# Revit family: IS_Tipica_T2378_BIM_FR
name_source: partatom
category: Plumbing Fixtures
revit_build: Autodesk Revit 2017 (Build: 20160225_1515(x64)
units: mm (PartAtom-declared; Revit-internal decimal feet)

## family parameters
Always vertical = No
Cut with Voids When Loaded = No
OmniClass Number = 23.45.05.14.21.11
OmniClass Title = Bath/Shower Units
Part Type = Normal
Room Calculation Point = No
Round Connector Dimension = Use Diameter
Shared = No
Work Plane-Based = No

## types (2) — shared parameters
Accessoires = www.idealspec.fr
Auteur = Ideal Standard
BIMobject category = Shower screens
BIMobject category code = sanitary-shower-screens
BIMobject main category = Sanitary
BIMobject main category code = sanitary
BOSUseNativeGeometries = 1
Brand url = www.idealspec.fr
Caractéristiques = TIPICA A SHW ENCL 80X80 TRANSP.WHITE
CodeBarre = 8014140362234
Conformité = NF
ConseilsDInstallation = 0
Couleur = Argent, clair
Date of publishing = 2018_07_24
DateDeCréation = 2018_07_24
Description = TIPICA A Cabine de douche 80 x 80 cm verre transparent
Dimensions = 820 x 820 x 1850 mm
EAN code = https://8014140362234
Edition number = 1
Espace = Interne
Finition = Argent, clair
Forme = Complexe
Hauteur = 1850 mm  [stored 6.06955 ft]
IFC Classification = Sanitary Terminal
IfcExportAs = SHOWER ENCLOSURES
IfcExportType = IfcSanitaryTerminalType
InformationsProduit = www.idealspec.fr
Installation instructions = http://www.idealspec.fr
Largeur = 820 mm
Longueur = 820 mm
Manufacturer name = Ideal Standard
Marque = Ideal Standard
Material main = Glass
Matériel = Glass
NBS Reference Code = 35-06-79
NBS Reference Description = Shower Enclosures
Nominal height = 1850
Nominal width = 795
OmniClass Code = 23-31 17 00
OmniClass Description = Showers
Product Guid = fd2bb281-8874-41ba-9d1a-fc2fd3af9e73
Product SKU = T2378
Product certification = http://www.idealspec.fr
Product data url = https://bimobject.com
Product family = Sanitary
Product group = Shower enclosures
Product name = TIPICA A SHW ENCL 80X80 TRANSP.WHITE
Product url = http://www.idealstandard.it
QR code = http://bimobject.com
Raccordement = Plomberie
Receveur = No
Révision = 1
Technical description = http://www.idealspec.fr
TypeDeDouche = Enclosure
URL = www.idealspec.fr
Uniclass 1.4 Code = L72142
Uniclass 1.4 Description = Shower screens, curtains
Uniclass 2.0 Code = PR-35-06-79
Uniclass 2.0 Description = Shower Enclosures
Uniclass 2015 Code = Pr_40_20_06_79
Uniclass 2015 Name = Shower enclosures
Uniclass2015Code = Pr_40_20_06_79
Uniclass2015Title = Shower enclosures
Uniclass2015Version = Products v1.1
UnitéDeMesure = Millimètres
UnitéDeTemps = An
UnitéMonétaire = €
UrlDuFabricant = www.idealspec.fr
Version = 1
Weight Net (Kg) = 20.5
Youtube clip = http://www.idealspec.fr
zero-valued in all types: Cost, CoûtDeRemplacement, Profondeur

## per-type parameters (varying)
| type | Bim-NomDuProjet | Model |
| T2378YB - TIPICA A CABINE DOUCHE 80X80 TSP ARG BR | ISI_IdealStandard_ShowerEnclosures_TIPICA_T2378YB | T2378YB |
| T2378AC - TIPICA A CAB 80X80 TRANSP. BLC | ISI_IdealStandard_ShowerEnclosures_TIPICA_T2378AC | T2378AC |

note: [stored X ft] marks values corroborated as IEEE doubles in the binary element streams (Revit-internal decimal feet)

## geometry (parser evidence)
native form markers: Sweep x3
no freeform markers — native parametric forms only
